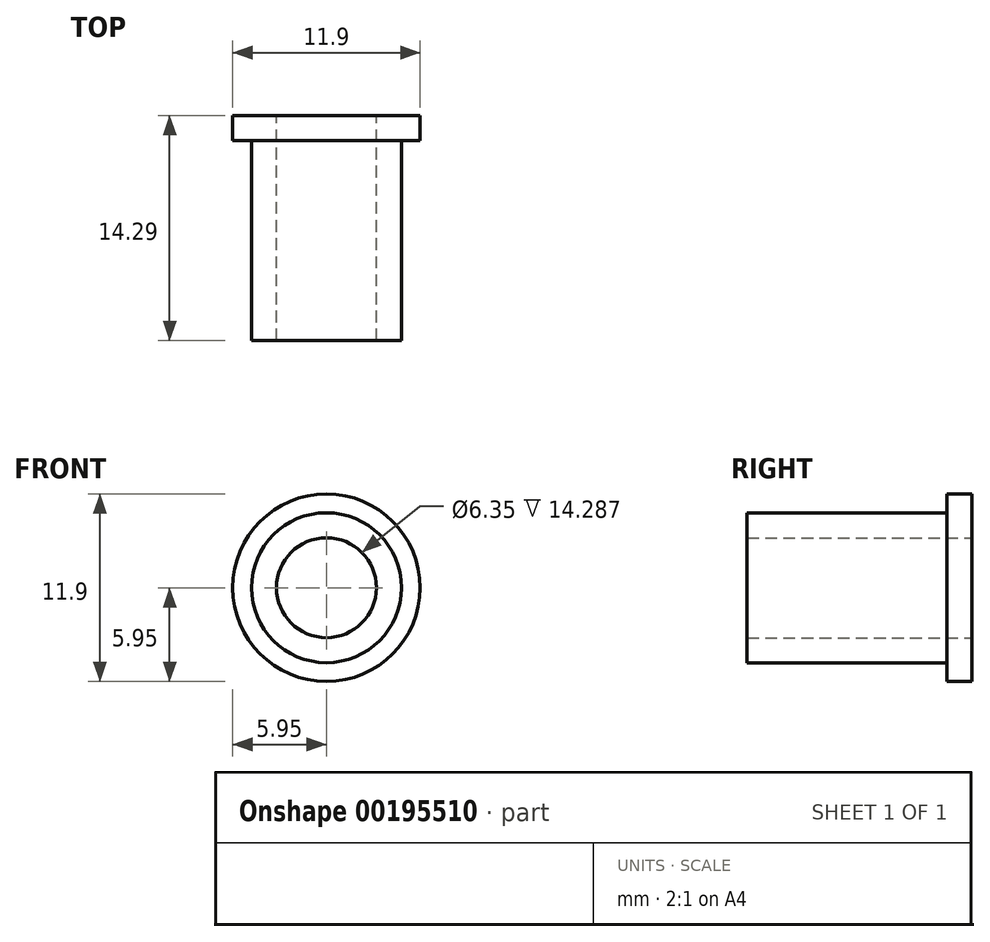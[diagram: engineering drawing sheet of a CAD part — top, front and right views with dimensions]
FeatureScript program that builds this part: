
annotation { "Feature Type Name" : "Feature", "Feature Type Description" : "" }
export const myFeature = defineFeature(function(context is Context, id is Id, definition is map)
    precondition{}
    {
        {
            var Q0;
            Q0=qCreatedBy(makeId("Front.planeOp"),FACE);
            var sketch = newSketch(context, id + "F0", { "sketchPlane" : qUnion([Q0])});
            skCircle(sketch, "E0", {"center": v(0, 0) * mm, "radius": 4.76 * mm});
            skCircle(sketch, "E1", {"center": v(0, 0) * mm, "radius": 3.18 * mm});
            skSolve(sketch);
        }
        {
            var Q0;
            Q0=qSketchRegion(id+"F0",true);
            extrude(context, id + "F1", {"entities" : qUnion([Q0]), "depth" : 12.7 * mm});
        }
        {
            var Q0;
            Q0=makeQuery(id+"F1.opExtrude","CAP_FACE",FACE,{"disambiguationData":[OSD([sQuery(id+"F0.wireOp",EDGE,"E0"),sQuery(id+"F0.wireOp",EDGE,"E1")])],"isStart":true});
            var sketch = newSketch(context, id + "F2", { "sketchPlane" : qUnion([Q0])});
            skCircle(sketch, "E2", {"center": v(0, 0) * mm, "radius": 5.95 * mm});
            skCircle(sketch, "E3", {"center": v(0, 0) * mm, "radius": 3.18 * mm});
            skSolve(sketch);
        }
        {
            var Q0;
            Q0=makeQuery(id+"F2.imprint","IMPRINT",FACE,{"disambiguationData":[TD([[makeQuery(id+"F2.imprint","IMPRINT",EDGE,{"derivedFrom":sQuery(id+"F2.wireOp",EDGE,"E2")}),1.0]])]});
            var Q1;
            Q1=makeQuery(id+"F2.imprint","IMPRINT",FACE,{"disambiguationData":[TD([[makeQuery(id+"F2.imprint","IMPRINT",EDGE,{"derivedFrom":sQuery(id+"F2.wireOp",EDGE,"E3")}),1.0]])]});
            extrude(context, id + "F3", {"entities" : qUnion([Q0, Q1]), "operationType" : NewBodyOperationType.ADD, "depth" : 1.59 * mm});
        }
    });
